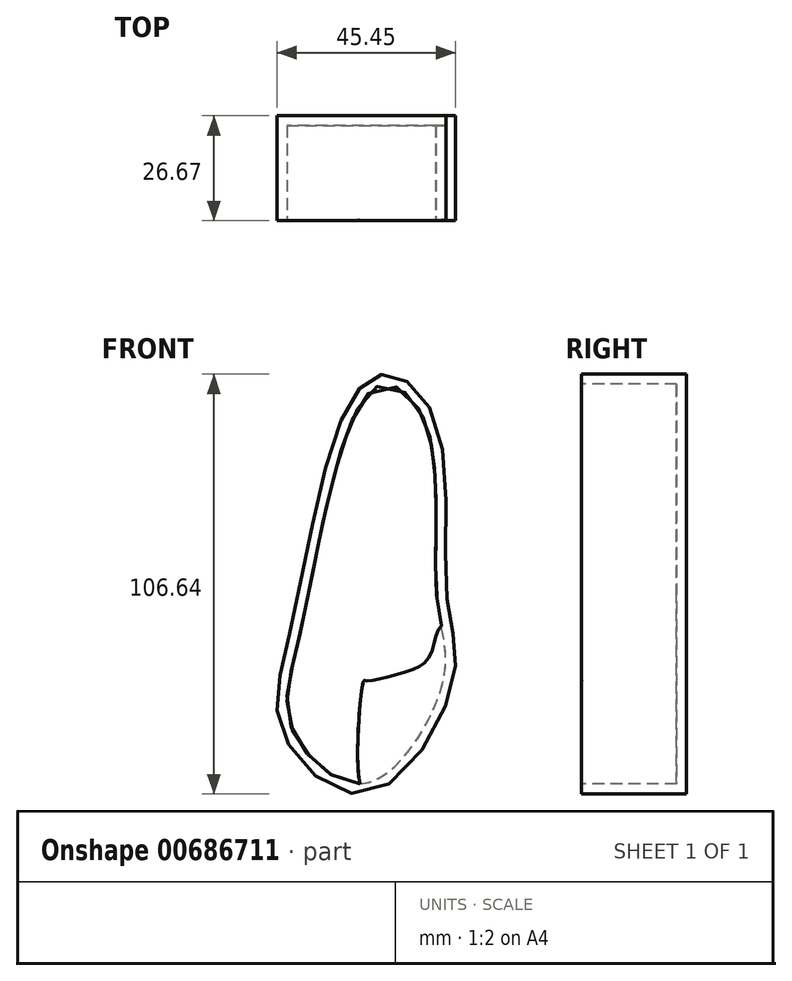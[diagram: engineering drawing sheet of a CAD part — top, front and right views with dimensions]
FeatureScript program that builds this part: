
annotation { "Feature Type Name" : "Feature", "Feature Type Description" : "" }
export const myFeature = defineFeature(function(context is Context, id is Id, definition is map)
    precondition{}
    {
        {
            var Q0;
            Q0=qCreatedBy(makeId("Front.planeOp"),FACE);
            var sketch = newSketch(context, id + "F0", { "sketchPlane" : qUnion([Q0])});
            skFitSpline(sketch, "E0", {"points": [v(-28.96, 11.88) * mm, v(-30.65, -13.35) * mm, v(-9.28, -28.55) * mm, v(12.65, 0) * mm, v(10.97, 21.72) * mm, v(8.15, 65.9) * mm, v(-4.78, 77.9) * mm, v(-16.03, 65.66) * mm, v(-28.96, 11.88) * mm]});
            skSolve(sketch);
        }
        {
            var Q0;
            Q0 = qSketchRegion(id + "F0", true);
            extrude(context, id + "F1", {"entities" : qUnion([Q0]), "depth" : 25.4 * mm, "offsetDistance" : 25.4 * mm});
        }
        {
            var Q0;
            Q0=makeQuery(id+"F1.opExtrude","CAP_FACE",FACE,{"disambiguationData":[OSD([sQuery(id+"F0.wireOp",EDGE,"E0")])],"isStart":false});
            extrude(context, id + "F2", {"entities" : qUnion([Q0]), "operationType" : NewBodyOperationType.ADD, "depth" : 1.27 * mm, "offsetDistance" : 25.4 * mm});
        }
        {
            var Q0;
            Q0=makeQuery(id+"F2.opExtrude","CAP_FACE",FACE,{"disambiguationData":[OSD([sQuery(id+"F0.wireOp",EDGE,"E0")])],"isStart":false});
            shell(context, id + "F3", {"entities" : qUnion([Q0]), "thickness" : 2.54 * mm});
        }
        {
            var Q0;
            Q0=makeQuery(id+"F2.opExtrude","CAP_FACE",FACE,{"disambiguationData":[OSD([sQuery(id+"F0.wireOp",EDGE,"E0")])],"isStart":false});
            var sketch = newSketch(context, id + "F4", { "sketchPlane" : qUnion([Q0])});
            skFitSpline(sketch, "E1", {"points": [v(-10.07, -28.66) * mm, v(-10.15, 0) * mm, v(-9.67, 0) * mm, v(0, 2.15) * mm, v(6.65, 6.32) * mm, v(9.57, 13.98) * mm, v(12.5, 12.2) * mm, v(12.15, -2.03) * mm, v(6.6, -14.62) * mm, v(-6.26, -27.6) * mm, v(-6.76, -27.8) * mm, v(-10.07, -28.66) * mm]});
            skSolve(sketch);
        }
        {
            var Q0;
            {var subQ0=sQuery(id+"F4.wireOp",EDGE,"E1");var subQ1=sQuery(id+"F0.wireOp",EDGE,"E0");var subQ2=makeQuery(id+"F3.opShell","OFFSET_EDGE",EDGE,{"disambiguationData":[OSD([subQ1]),TDD([makeQuery(id+"F2.opExtrude","CAP_EDGE",EDGE,{"disambiguationData":[OSD([subQ1])],"isStart":false})])]});var subQ3=makeQuery(id+"F4.imprint","INTERSECT",VERTEX,{"disambiguationData":[OD(0.0)],"derivedFrom":[subQ2,subQ0]});Q0=makeQuery(id+"F4.imprint","IMPRINT",FACE,{"disambiguationData":[TD([[makeQuery(id+"F4.imprint","IMPRINT",EDGE,{"disambiguationData":[TD([[subQ3,-1.0]])],"derivedFrom":subQ0}),-1.0]])]});}
            extrude(context, id + "F5", {"entities" : qUnion([Q0]), "operationType" : NewBodyOperationType.ADD, "oppositeDirection" : true, "depth" : 0.25 * mm, "offsetDistance" : 25.4 * mm});
        }
    });
